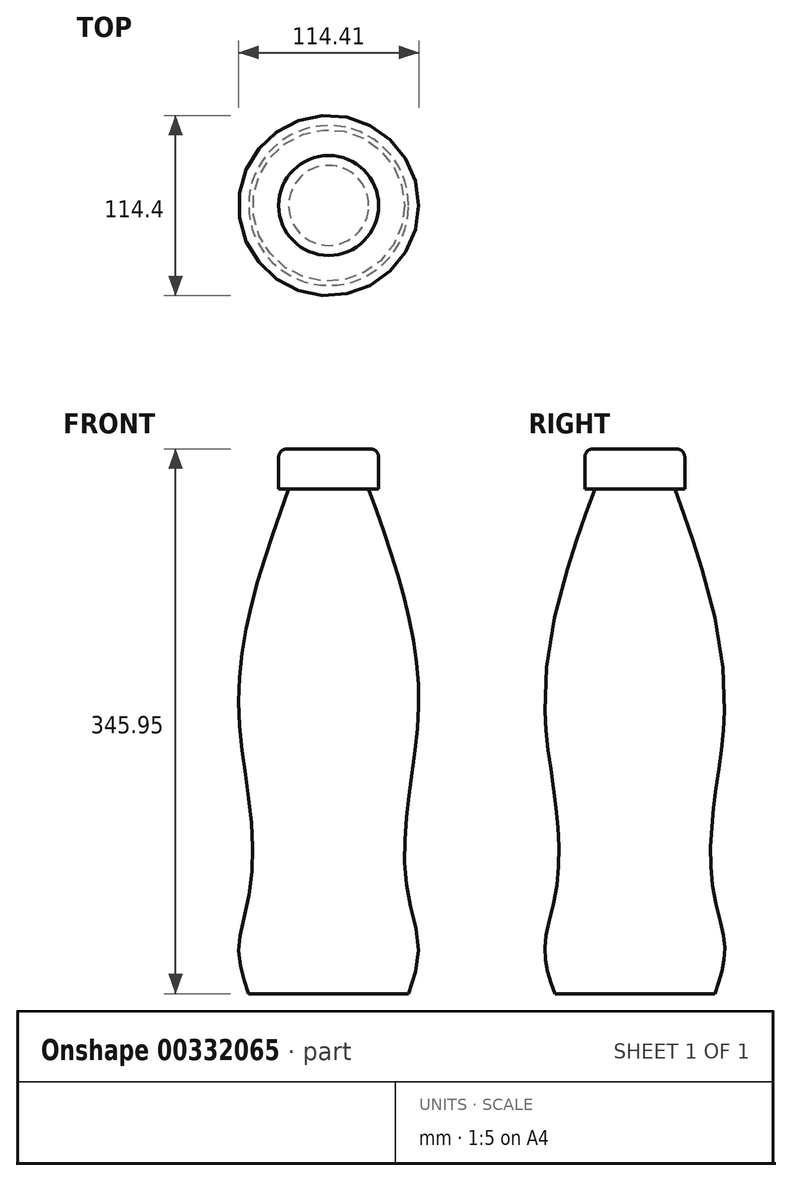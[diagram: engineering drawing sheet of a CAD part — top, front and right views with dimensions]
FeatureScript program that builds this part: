
annotation { "Feature Type Name" : "Feature", "Feature Type Description" : "" }
export const myFeature = defineFeature(function(context is Context, id is Id, definition is map)
    precondition{}
    {
        {
            var Q0;
            Q0=qCreatedBy(makeId("Top.planeOp"),FACE);
            cPlane(context, id + "F0", {"entities" : qUnion([Q0]), "cplaneType" : CPlaneType.OFFSET, "offset" : 25.9 * mm, "width" : 152.4 * mm, "height" : 152.4 * mm});
        }
        {
            var Q0;
            Q0=qCreatedBy(id+"F0.planeOp",FACE);
            cPlane(context, id + "F1", {"entities" : qUnion([Q0]), "cplaneType" : CPlaneType.OFFSET, "offset" : 35.05 * mm, "width" : 152.4 * mm, "height" : 152.4 * mm});
        }
        {
            var Q0;
            Q0=qCreatedBy(makeId("Top.planeOp"),FACE);
            var sketch = newSketch(context, id + "F2", { "sketchPlane" : qUnion([Q0])});
            skCircle(sketch, "E0", {"center": v(0, 0) * mm, "radius": 50.8 * mm});
            skSolve(sketch);
        }
        {
            var Q0;
            Q0=qCreatedBy(id+"F0.planeOp",FACE);
            var sketch = newSketch(context, id + "F3", { "sketchPlane" : qUnion([Q0])});
            skCircle(sketch, "E1", {"center": v(0, 0) * mm, "radius": 57.15 * mm});
            skSolve(sketch);
        }
        {
            var Q0;
            Q0=qCreatedBy(id+"F1.planeOp",FACE);
            var sketch = newSketch(context, id + "F4", { "sketchPlane" : qUnion([Q0])});
            skCircle(sketch, "E2", {"center": v(0, 0) * mm, "radius": 50.8 * mm});
            skSolve(sketch);
        }
        {
            var Q0;
            Q0=qCreatedBy(id+"F1.planeOp",FACE);
            cPlane(context, id + "F5", {"entities" : qUnion([Q0]), "cplaneType" : CPlaneType.OFFSET, "offset" : 120.9 * mm, "width" : 152.4 * mm, "height" : 152.4 * mm});
        }
        {
            var Q0;
            Q0=qCreatedBy(id+"F5.planeOp",FACE);
            var sketch = newSketch(context, id + "F6", { "sketchPlane" : qUnion([Q0])});
            skCircle(sketch, "E3", {"center": v(0, 0) * mm, "radius": 57.15 * mm});
            skSolve(sketch);
        }
        {
            var Q0;
            Q0=qCreatedBy(id+"F5.planeOp",FACE);
            cPlane(context, id + "F7", {"entities" : qUnion([Q0]), "cplaneType" : CPlaneType.OFFSET, "offset" : 138.68 * mm, "width" : 152.4 * mm, "height" : 152.4 * mm});
        }
        {
            var Q0;
            Q0=qCreatedBy(id+"F7.planeOp",FACE);
            var sketch = newSketch(context, id + "F8", { "sketchPlane" : qUnion([Q0])});
            skCircle(sketch, "E4", {"center": v(0, 0) * mm, "radius": 25.4 * mm});
            skSolve(sketch);
        }
        {
            var Q0;
            Q0=makeQuery(id+"F8.imprint","IMPRINT",FACE,{"disambiguationData":[TD([[makeQuery(id+"F8.imprint","IMPRINT",EDGE,{"derivedFrom":sQuery(id+"F8.wireOp",EDGE,"E4")}),1.0]])]});
            var Q1;
            Q1=makeQuery(id+"F6.imprint","IMPRINT",FACE,{"disambiguationData":[TD([[makeQuery(id+"F6.imprint","IMPRINT",EDGE,{"derivedFrom":sQuery(id+"F6.wireOp",EDGE,"E3")}),1.0]])]});
            var Q2;
            Q2=makeQuery(id+"F4.imprint","IMPRINT",FACE,{"disambiguationData":[TD([[makeQuery(id+"F4.imprint","IMPRINT",EDGE,{"derivedFrom":sQuery(id+"F4.wireOp",EDGE,"E2")}),1.0]])]});
            var Q3;
            Q3=makeQuery(id+"F3.imprint","IMPRINT",FACE,{"disambiguationData":[TD([[makeQuery(id+"F3.imprint","IMPRINT",EDGE,{"derivedFrom":sQuery(id+"F3.wireOp",EDGE,"E1")}),1.0]])]});
            var Q4;
            Q4=makeQuery(id+"F2.imprint","IMPRINT",FACE,{"disambiguationData":[TD([[makeQuery(id+"F2.imprint","IMPRINT",EDGE,{"derivedFrom":sQuery(id+"F2.wireOp",EDGE,"E0")}),1.0]])]});
            loft(context, id + "F9", {"sheetProfilesArray" : [{ "sheetProfileEntities" : qUnion([Q0]) }, { "sheetProfileEntities" : qUnion([Q1]) }, { "sheetProfileEntities" : qUnion([Q2]) }, { "sheetProfileEntities" : qUnion([Q3]) }, { "sheetProfileEntities" : qUnion([Q4]) }]});
        }
        {
            var Q0;
            Q0=qCreatedBy(id+"F7.planeOp",FACE);
            var sketch = newSketch(context, id + "F10", { "sketchPlane" : qUnion([Q0])});
            skCircle(sketch, "E5", {"center": v(0, 0) * mm, "radius": 31.75 * mm});
            skSolve(sketch);
        }
        {
            var Q0;
            Q0 = qSketchRegion(id + "F10", true);
            extrude(context, id + "F11", {"entities" : qUnion([Q0]), "operationType" : NewBodyOperationType.ADD, "depth" : 25.4 * mm});
        }
        {
            var Q0;
            Q0=makeQuery(id+"F11.opExtrude","CAP_EDGE",EDGE,{"disambiguationData":[OSD([sQuery(id+"F10.wireOp",EDGE,"E5")])],"isStart":false});
            fillet(context, id + "F12", {"entities" : qUnion([Q0]), "radius" : 5.08 * mm, "tangentPropagation" : true, "allowEdgeOverflow" : false});
        }
        {
            var Q0;
            Q0=qCreatedBy(makeId("Right.planeOp"),FACE);
            var sketch = newSketch(context, id + "F13", { "sketchPlane" : qUnion([Q0])});
            skLineSegment(sketch, "E6", {"start": v(-82.2, 0) * mm, "end": v(111.65, 0) * mm, "construction": true});
            skSolve(sketch);
        }
    });
